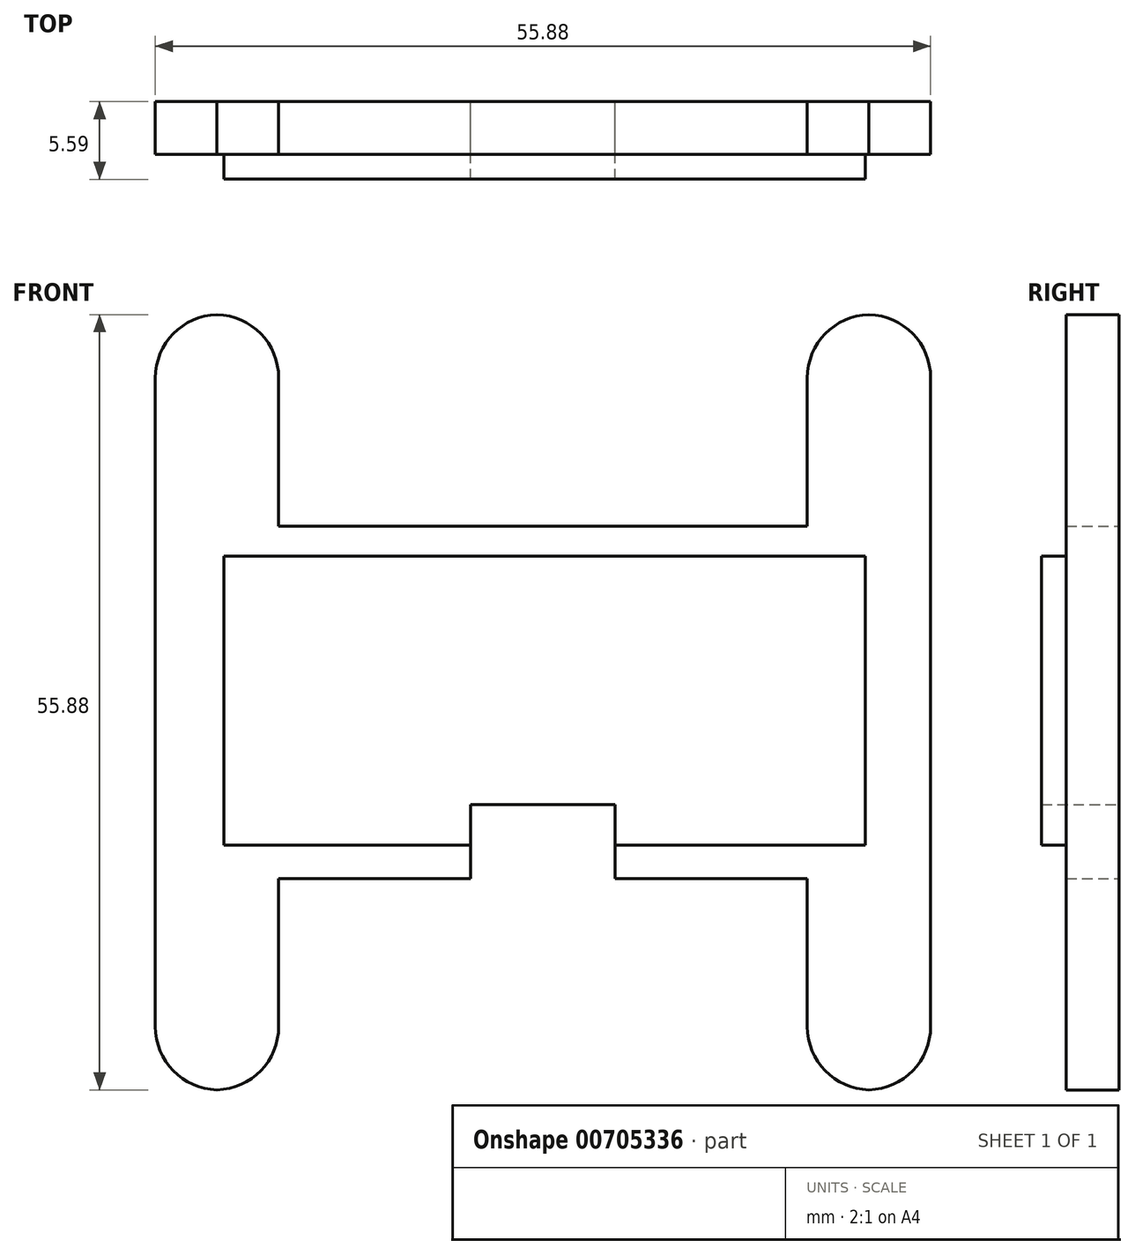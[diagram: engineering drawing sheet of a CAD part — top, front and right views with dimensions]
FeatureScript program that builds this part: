
annotation { "Feature Type Name" : "Feature", "Feature Type Description" : "" }
export const myFeature = defineFeature(function(context is Context, id is Id, definition is map)
    precondition{}
    {
        {
            var Q0;
            Q0=qCreatedBy(makeId("Front.planeOp"),FACE);
            var sketch = newSketch(context, id + "F0", { "sketchPlane" : qUnion([Q0])});
            skLineSegment(sketch, "E0.bottom", {"start": v(-19.9, 13.24) * mm, "end": v(35.97, 13.24) * mm});
            skLineSegment(sketch, "E0.top", {"start": v(-19.9, -12.16) * mm, "end": v(35.97, -12.16) * mm});
            skLineSegment(sketch, "E0.left", {"start": v(-19.9, 13.24) * mm, "end": v(-19.9, -12.16) * mm});
            skLineSegment(sketch, "E0.right", {"start": v(35.97, 13.24) * mm, "end": v(35.97, -12.16) * mm});
            skSolve(sketch);
        }
        {
            var Q0;
            Q0=makeQuery(id+"F0.imprint","IMPRINT",FACE,{"disambiguationData":[TD([[makeQuery(id+"F0.imprint","IMPRINT",EDGE,{"derivedFrom":sQuery(id+"F0.wireOp",EDGE,"E0.bottom")}),-1.0]])]});
            extrude(context, id + "F1", {"entities" : qUnion([Q0]), "depth" : 3.8 * mm, "offsetDistance" : 25.4 * mm});
        }
        {
            var Q0;
            Q0=makeQuery(id+"F1.opExtrude","CAP_FACE",FACE,{"disambiguationData":[OSD([sQuery(id+"F0.wireOp",EDGE,"E0.bottom"),sQuery(id+"F0.wireOp",EDGE,"E0.top"),sQuery(id+"F0.wireOp",EDGE,"E0.left"),sQuery(id+"F0.wireOp",EDGE,"E0.right")])],"isStart":false});
            var sketch = newSketch(context, id + "F2", { "sketchPlane" : qUnion([Q0])});
            skLineSegment(sketch, "E1.bottom", {"start": v(-14.95, 11.08) * mm, "end": v(31.27, 11.08) * mm});
            skLineSegment(sketch, "E1.top", {"start": v(-14.95, -9.75) * mm, "end": v(31.27, -9.75) * mm});
            skLineSegment(sketch, "E1.left", {"start": v(-14.95, 11.08) * mm, "end": v(-14.95, -9.75) * mm});
            skLineSegment(sketch, "E1.right", {"start": v(31.27, 11.08) * mm, "end": v(31.27, -9.75) * mm});
            skSolve(sketch);
        }
        {
            var Q0;
            Q0 = qSketchRegion(id + "F2", true);
            extrude(context, id + "F3", {"entities" : qUnion([Q0]), "operationType" : NewBodyOperationType.ADD, "depth" : 1.78 * mm, "offsetDistance" : 25.4 * mm});
        }
        {
            var Q0;
            Q0=makeQuery(id+"F0.imprint","IMPRINT",FACE,{"disambiguationData":[TD([[makeQuery(id+"F0.imprint","IMPRINT",EDGE,{"derivedFrom":sQuery(id+"F0.wireOp",EDGE,"E0.bottom")}),-1.0]])]});
            var sketch = newSketch(context, id + "F4", { "sketchPlane" : qUnion([Q0])});
            skLineSegment(sketch, "E2.bottom", {"start": v(13.24, -6.83) * mm, "end": v(2.83, -6.83) * mm});
            skLineSegment(sketch, "E2.top", {"start": v(13.24, -15.95) * mm, "end": v(2.83, -15.95) * mm});
            skLineSegment(sketch, "E2.left", {"start": v(13.24, -6.83) * mm, "end": v(13.24, -15.95) * mm});
            skLineSegment(sketch, "E2.right", {"start": v(2.83, -6.83) * mm, "end": v(2.83, -15.95) * mm});
            skSolve(sketch);
        }
        {
            var Q0;
            Q0 = qSketchRegion(id + "F4", true);
            extrude(context, id + "F5", {"entities" : qUnion([Q0]), "operationType" : NewBodyOperationType.REMOVE, "depth" : 25.4 * mm, "offsetDistance" : 25.4 * mm});
        }
        {
            var Q0;
            Q0=makeQuery(id+"F0.imprint","IMPRINT",FACE,{"disambiguationData":[TD([[makeQuery(id+"F0.imprint","IMPRINT",EDGE,{"derivedFrom":sQuery(id+"F0.wireOp",EDGE,"E0.bottom")}),-1.0]])]});
            var sketch = newSketch(context, id + "F6", { "sketchPlane" : qUnion([Q0])});
            skLineSegment(sketch, "E3.bottom", {"start": v(35.97, 13.24) * mm, "end": v(27.08, 13.24) * mm});
            skLineSegment(sketch, "E3.top", {"start": v(35.97, 28.48) * mm, "end": v(27.08, 28.48) * mm});
            skLineSegment(sketch, "E3.left", {"start": v(35.97, 13.24) * mm, "end": v(35.97, 28.48) * mm});
            skLineSegment(sketch, "E3.right", {"start": v(27.08, 13.24) * mm, "end": v(27.08, 28.48) * mm});
            skSolve(sketch);
        }
        {
            var Q0;
            Q0=makeQuery(id+"F6.imprint","IMPRINT",FACE,{"disambiguationData":[TD([[makeQuery(id+"F6.imprint","IMPRINT",EDGE,{"derivedFrom":sQuery(id+"F6.wireOp",EDGE,"E3.bottom")}),1.0]])]});
            extrude(context, id + "F7", {"entities" : qUnion([Q0]), "operationType" : NewBodyOperationType.ADD, "depth" : 3.8 * mm, "offsetDistance" : 25.4 * mm});
        }
        {
            var Q0;
            Q0=makeQuery(id+"F7.opExtrude","SWEPT_EDGE",EDGE,{"disambiguationData":[OSD([sQuery(id+"F6.wireOp",EDGE,"E3.top"),sQuery(id+"F6.wireOp",EDGE,"E3.left")])]});
            var Q1;
            Q1=makeQuery(id+"F7.opExtrude","SWEPT_EDGE",EDGE,{"disambiguationData":[OSD([sQuery(id+"F6.wireOp",EDGE,"E3.top"),sQuery(id+"F6.wireOp",EDGE,"E3.right")])]});
            fillet(context, id + "F8", {"entities" : qUnion([Q0, Q1]), "radius" : 4.57 * mm, "tangentPropagation" : true, "allowEdgeOverflow" : false});
        }
        {
            var Q0;
            Q0=makeQuery(id+"F0.imprint","IMPRINT",FACE,{"disambiguationData":[TD([[makeQuery(id+"F0.imprint","IMPRINT",EDGE,{"derivedFrom":sQuery(id+"F0.wireOp",EDGE,"E0.bottom")}),-1.0]])]});
            var sketch = newSketch(context, id + "F9", { "sketchPlane" : qUnion([Q0])});
            skLineSegment(sketch, "E4", {"start": v(8.03, 12.5) * mm, "end": v(8.03, -7.5) * mm});
            skLineSegment(sketch, "E5", {"start": v(34.38, 0) * mm, "end": v(-21.75, 0) * mm});
            skSolve(sketch);
        }
        {
            var Q0;
            {var subQ1=makeQuery(id+"F0.imprint","IMPRINT",EDGE,{"derivedFrom":sQuery(id+"F0.wireOp",EDGE,"E0.top")});Q0=makeQuery(id+"F9.imprint","IMPRINT",FACE,{"disambiguationData":[TD([[makeQuery(id+"F9.imprint","IMPRINT",EDGE,{"derivedFrom":subQ1}),1.0]])]});}
            var sketch = newSketch(context, id + "F10", { "sketchPlane" : qUnion([Q0])});
            skLineSegment(sketch, "E6.bottom", {"start": v(-19.9, 13.24) * mm, "end": v(-11.02, 13.24) * mm});
            skLineSegment(sketch, "E6.top", {"start": v(-19.9, 28.48) * mm, "end": v(-11.02, 28.48) * mm});
            skLineSegment(sketch, "E6.left", {"start": v(-19.9, 13.24) * mm, "end": v(-19.9, 28.48) * mm});
            skLineSegment(sketch, "E6.right", {"start": v(-11.02, 13.24) * mm, "end": v(-11.02, 28.48) * mm});
            skSolve(sketch);
        }
        {
            var Q0;
            Q0=makeQuery(id+"F10.imprint","IMPRINT",FACE,{"disambiguationData":[TD([[makeQuery(id+"F10.imprint","IMPRINT",EDGE,{"derivedFrom":sQuery(id+"F10.wireOp",EDGE,"E6.bottom")}),1.0]])]});
            extrude(context, id + "F11", {"entities" : qUnion([Q0]), "operationType" : NewBodyOperationType.ADD, "depth" : 3.8 * mm, "offsetDistance" : 25.4 * mm});
        }
        {
            var Q0;
            Q0=makeQuery(id+"F11.opExtrude","SWEPT_EDGE",EDGE,{"disambiguationData":[OSD([sQuery(id+"F10.wireOp",EDGE,"E6.top"),sQuery(id+"F10.wireOp",EDGE,"E6.left")])]});
            var Q1;
            Q1=makeQuery(id+"F11.opExtrude","SWEPT_EDGE",EDGE,{"disambiguationData":[OSD([sQuery(id+"F10.wireOp",EDGE,"E6.top"),sQuery(id+"F10.wireOp",EDGE,"E6.right")])]});
            fillet(context, id + "F12", {"entities" : qUnion([Q0, Q1]), "radius" : 4.57 * mm, "tangentPropagation" : true, "allowEdgeOverflow" : false});
        }
        {
            var Q0;
            {var subQ1=makeQuery(id+"F0.imprint","IMPRINT",EDGE,{"derivedFrom":sQuery(id+"F0.wireOp",EDGE,"E0.top")});Q0=makeQuery(id+"F9.imprint","IMPRINT",FACE,{"disambiguationData":[TD([[makeQuery(id+"F9.imprint","IMPRINT",EDGE,{"derivedFrom":subQ1}),1.0]])]});}
            var sketch = newSketch(context, id + "F13", { "sketchPlane" : qUnion([Q0])});
            skLineSegment(sketch, "E7.bottom", {"start": v(35.97, -12.16) * mm, "end": v(27.08, -12.16) * mm});
            skLineSegment(sketch, "E7.top", {"start": v(35.97, -27.4) * mm, "end": v(27.08, -27.4) * mm});
            skLineSegment(sketch, "E7.left", {"start": v(35.97, -12.16) * mm, "end": v(35.97, -27.4) * mm});
            skLineSegment(sketch, "E7.right", {"start": v(27.08, -12.16) * mm, "end": v(27.08, -27.4) * mm});
            skSolve(sketch);
        }
        {
            var Q0;
            Q0 = qSketchRegion(id + "F13", true);
            extrude(context, id + "F14", {"entities" : qUnion([Q0]), "operationType" : NewBodyOperationType.ADD, "depth" : 3.8 * mm, "offsetDistance" : 25.4 * mm});
        }
        {
            var Q0;
            Q0=makeQuery(id+"F14.opExtrude","SWEPT_EDGE",EDGE,{"disambiguationData":[OSD([sQuery(id+"F13.wireOp",EDGE,"E7.top"),sQuery(id+"F13.wireOp",EDGE,"E7.left")])]});
            var Q1;
            Q1=makeQuery(id+"F14.opExtrude","SWEPT_EDGE",EDGE,{"disambiguationData":[OSD([sQuery(id+"F13.wireOp",EDGE,"E7.top"),sQuery(id+"F13.wireOp",EDGE,"E7.right")])]});
            fillet(context, id + "F15", {"entities" : qUnion([Q0, Q1]), "radius" : 4.57 * mm, "tangentPropagation" : true, "allowEdgeOverflow" : false});
        }
        {
            var Q0;
            {var subQ1=makeQuery(id+"F0.imprint","IMPRINT",EDGE,{"derivedFrom":sQuery(id+"F0.wireOp",EDGE,"E0.top")});Q0=makeQuery(id+"F9.imprint","IMPRINT",FACE,{"disambiguationData":[TD([[makeQuery(id+"F9.imprint","IMPRINT",EDGE,{"derivedFrom":subQ1}),1.0]])]});}
            var sketch = newSketch(context, id + "F16", { "sketchPlane" : qUnion([Q0])});
            skLineSegment(sketch, "E8.bottom", {"start": v(-19.9, -12.16) * mm, "end": v(-11.02, -12.16) * mm});
            skLineSegment(sketch, "E8.top", {"start": v(-19.9, -27.4) * mm, "end": v(-11.02, -27.4) * mm});
            skLineSegment(sketch, "E8.left", {"start": v(-19.9, -12.16) * mm, "end": v(-19.9, -27.4) * mm});
            skLineSegment(sketch, "E8.right", {"start": v(-11.02, -12.16) * mm, "end": v(-11.02, -27.4) * mm});
            skSolve(sketch);
        }
        {
            var Q0;
            Q0=makeQuery(id+"F16.imprint","IMPRINT",FACE,{"disambiguationData":[TD([[makeQuery(id+"F16.imprint","IMPRINT",EDGE,{"derivedFrom":sQuery(id+"F16.wireOp",EDGE,"E8.bottom")}),-1.0]])]});
            extrude(context, id + "F17", {"entities" : qUnion([Q0]), "operationType" : NewBodyOperationType.ADD, "depth" : 3.8 * mm, "offsetDistance" : 25.4 * mm});
        }
        {
            var Q0;
            Q0=makeQuery(id+"F17.opExtrude","SWEPT_EDGE",EDGE,{"disambiguationData":[OSD([sQuery(id+"F16.wireOp",EDGE,"E8.top"),sQuery(id+"F16.wireOp",EDGE,"E8.left")])]});
            var Q1;
            Q1=makeQuery(id+"F17.opExtrude","SWEPT_EDGE",EDGE,{"disambiguationData":[OSD([sQuery(id+"F16.wireOp",EDGE,"E8.top"),sQuery(id+"F16.wireOp",EDGE,"E8.right")])]});
            fillet(context, id + "F18", {"entities" : qUnion([Q0, Q1]), "radius" : 4.57 * mm, "tangentPropagation" : true, "allowEdgeOverflow" : false});
        }
    });
